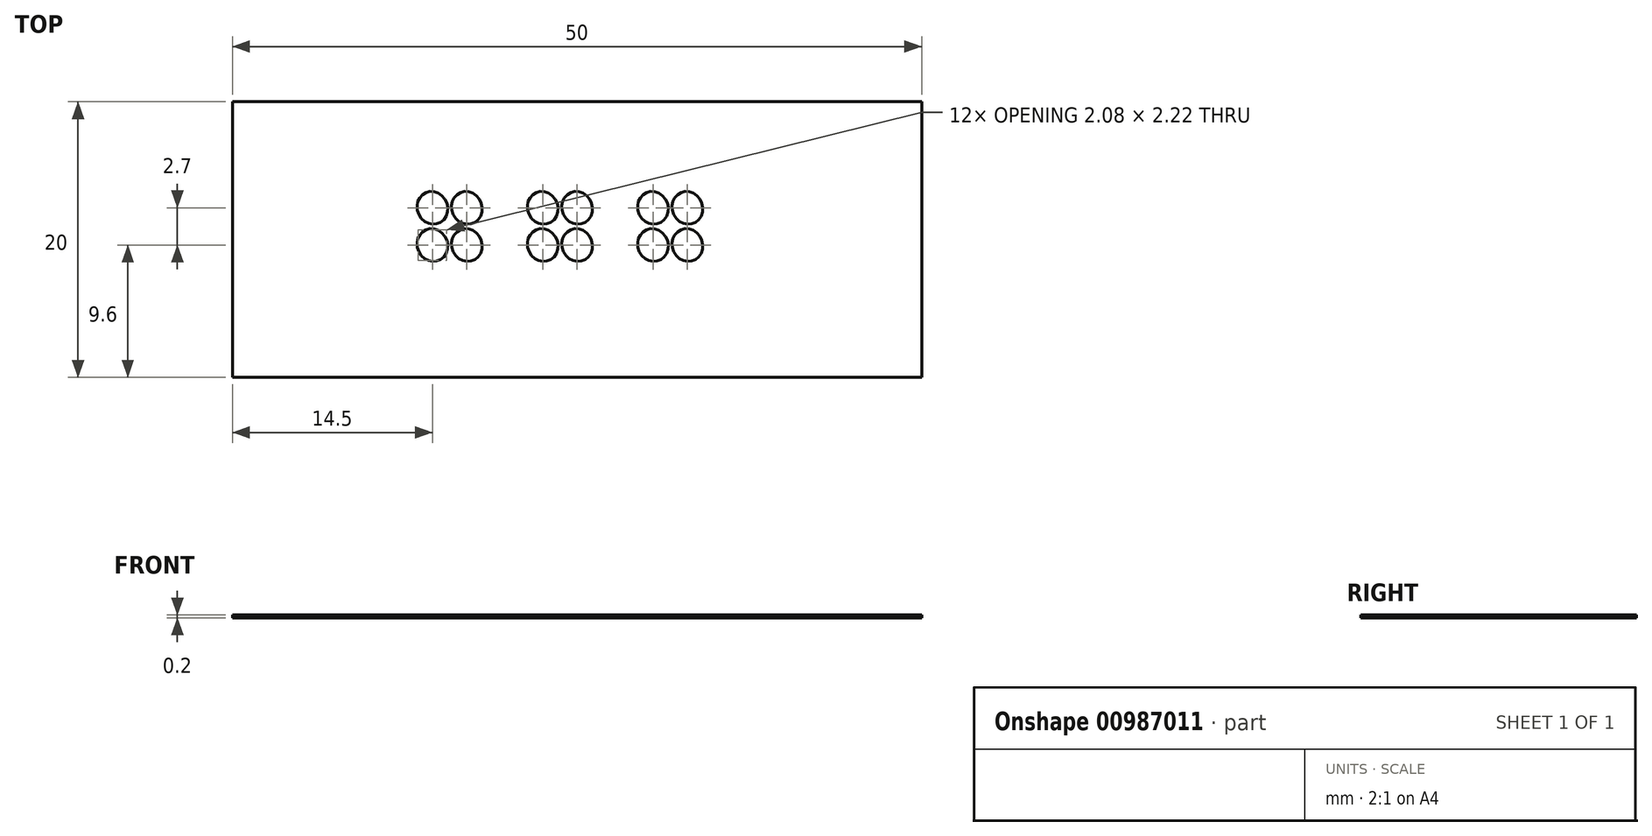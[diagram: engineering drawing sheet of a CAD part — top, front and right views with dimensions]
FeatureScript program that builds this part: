
annotation { "Feature Type Name" : "Feature", "Feature Type Description" : "" }
export const myFeature = defineFeature(function(context is Context, id is Id, definition is map)
    precondition{}
    {
        {
            var Q0;
            Q0=qCreatedBy(makeId("Top.planeOp"),FACE);
            var sketch = newSketch(context, id + "F0", { "sketchPlane" : qUnion([Q0])});
            skLineSegment(sketch, "E0.bottom", {"start": v(0, 0) * mm, "end": v(50, 0) * mm});
            skLineSegment(sketch, "E0.top", {"start": v(0, -20) * mm, "end": v(50, -20) * mm});
            skLineSegment(sketch, "E0.left", {"start": v(0, 0) * mm, "end": v(0, -20) * mm});
            skLineSegment(sketch, "E0.right", {"start": v(50, 0) * mm, "end": v(50, -20) * mm});
            skEllipse(sketch, "E1", {"center": v(14.5, -7.7) * mm, "majorRadius": 1.1 * mm, "minorRadius": 1.2 * mm, "majorAxis": v(0.93, 0.38)});
            skLineSegment(sketch, "E2.direction1", {"start": v(14.5, -7.7) * mm, "end": v(17, -7.7) * mm, "construction": true});
            skEllipse(sketch, "E3.0.1.0", {"center": v(17, -7.7) * mm, "majorRadius": 1.1 * mm, "minorRadius": 1.2 * mm, "majorAxis": v(0.93, 0.38)});
            skEllipse(sketch, "E4.1.0.0", {"center": v(17, -10.4) * mm, "majorRadius": 1.1 * mm, "minorRadius": 1.2 * mm, "majorAxis": v(0.93, 0.38)});
            skEllipse(sketch, "E4.1.0.1", {"center": v(14.5, -10.4) * mm, "majorRadius": 1.1 * mm, "minorRadius": 1.2 * mm, "majorAxis": v(0.93, 0.38)});
            skLineSegment(sketch, "E4.1.0.3", {"start": v(14.5, -10.4) * mm, "end": v(17, -10.4) * mm, "construction": true});
            skLineSegment(sketch, "E4.direction1", {"start": v(14.5, -7.7) * mm, "end": v(14.5, -10.4) * mm, "construction": true});
            skEllipse(sketch, "E5.1.0.0", {"center": v(25, -10.4) * mm, "majorRadius": 1.1 * mm, "minorRadius": 1.2 * mm, "majorAxis": v(0.93, 0.38)});
            skLineSegment(sketch, "E5.1.0.1", {"start": v(22.5, -7.7) * mm, "end": v(22.5, -10.4) * mm, "construction": true});
            skLineSegment(sketch, "E5.1.0.2", {"start": v(22.5, -10.4) * mm, "end": v(25, -10.4) * mm, "construction": true});
            skEllipse(sketch, "E5.1.0.3", {"center": v(22.5, -10.4) * mm, "majorRadius": 1.1 * mm, "minorRadius": 1.2 * mm, "majorAxis": v(0.93, 0.38)});
            skLineSegment(sketch, "E5.1.0.4", {"start": v(22.5, -7.7) * mm, "end": v(25, -7.7) * mm, "construction": true});
            skEllipse(sketch, "E5.1.0.5", {"center": v(25, -7.7) * mm, "majorRadius": 1.1 * mm, "minorRadius": 1.2 * mm, "majorAxis": v(0.93, 0.38)});
            skEllipse(sketch, "E5.1.0.6", {"center": v(22.5, -7.7) * mm, "majorRadius": 1.1 * mm, "minorRadius": 1.2 * mm, "majorAxis": v(0.93, 0.38)});
            skEllipse(sketch, "E5.2.0.0", {"center": v(33, -10.4) * mm, "majorRadius": 1.1 * mm, "minorRadius": 1.2 * mm, "majorAxis": v(0.93, 0.38)});
            skLineSegment(sketch, "E5.2.0.1", {"start": v(30.5, -7.7) * mm, "end": v(30.5, -10.4) * mm, "construction": true});
            skLineSegment(sketch, "E5.2.0.2", {"start": v(30.5, -10.4) * mm, "end": v(33, -10.4) * mm, "construction": true});
            skEllipse(sketch, "E5.2.0.3", {"center": v(30.5, -10.4) * mm, "majorRadius": 1.1 * mm, "minorRadius": 1.2 * mm, "majorAxis": v(0.93, 0.38)});
            skLineSegment(sketch, "E5.2.0.4", {"start": v(30.5, -7.7) * mm, "end": v(33, -7.7) * mm, "construction": true});
            skEllipse(sketch, "E5.2.0.5", {"center": v(33, -7.7) * mm, "majorRadius": 1.1 * mm, "minorRadius": 1.2 * mm, "majorAxis": v(0.93, 0.38)});
            skEllipse(sketch, "E5.2.0.6", {"center": v(30.5, -7.7) * mm, "majorRadius": 1.1 * mm, "minorRadius": 1.2 * mm, "majorAxis": v(0.93, 0.38)});
            skLineSegment(sketch, "E5.direction1", {"start": v(14.5, -10.4) * mm, "end": v(22.5, -10.4) * mm, "construction": true});
            skSolve(sketch);
        }
        {
            var Q0;
            Q0=makeQuery(id+"F0.imprint","IMPRINT",FACE,{"disambiguationData":[TD([[makeQuery(id+"F0.imprint","IMPRINT",EDGE,{"derivedFrom":sQuery(id+"F0.wireOp",EDGE,"E0.bottom")}),-1.0]])]});
            extrude(context, id + "F1", {"entities" : qUnion([Q0]), "depth" : 0.2 * mm, "offsetDistance" : 25.4 * mm});
        }
    });
